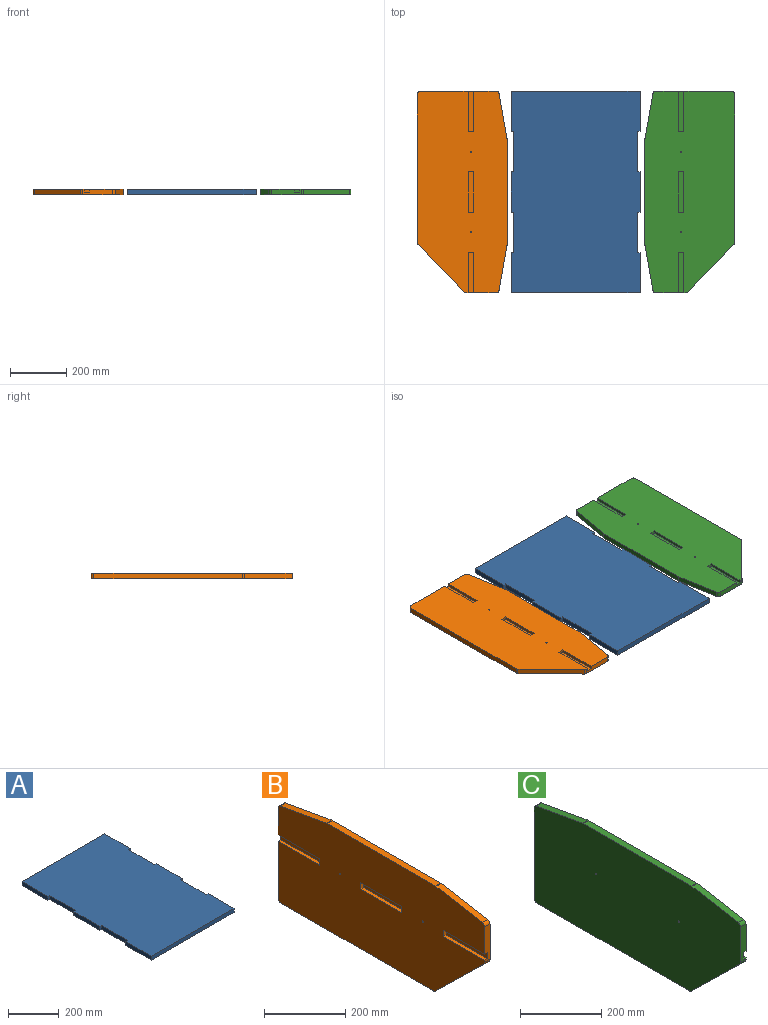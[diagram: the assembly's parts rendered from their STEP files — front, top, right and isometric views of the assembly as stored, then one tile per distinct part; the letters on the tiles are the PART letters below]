
ASSEMBLY  parts=3 mates=2
PART A: 22 faces, bbox 460x720x19 mm
  f0: plane 460x19mm, normal (0,-1,0), area 8740mm2, adj f2,f3,f4,f14
  f1: plane 19x10mm, normal (0,1,0), area 190mm2, adj f2,f3,f4,f5
  f2: plane 144x19mm, normal (-1,0,0), area 2736mm2, adj f0,f1,f3,f4
  f3: plane 720x460mm, normal (0,0,-1), area 325440mm2, adj f0,f1,f2,f5,f6,f7,f8,f9
  f4: plane 720x460mm, normal (0,0,1), area 325440mm2, adj f0,f1,f2,f5,f6,f7,f8,f9
  f5: plane 144x19mm, normal (-1,0,0), area 2736mm2, adj f1,f3,f4,f6
  f6: plane 19x10mm, normal (0,-1,0), area 190mm2, adj f3,f4,f5,f8
  f7: plane 19x10mm, normal (0,1,0), area 190mm2, adj f3,f4,f8,f9
  f8: plane 144x19mm, normal (-1,0,0), area 2736mm2, adj f3,f4,f6,f7
  f9: plane 144x19mm, normal (-1,0,0), area 2736mm2, adj f3,f4,f7,f10
  f10: plane 19x10mm, normal (0,-1,0), area 190mm2, adj f3,f4,f9,f12
  f11: plane 460x19mm, normal (0,1,0), area 8740mm2, adj f3,f4,f12,f21
  f12: plane 144x19mm, normal (-1,0,0), area 2736mm2, adj f3,f4,f10,f11
  f13: plane 19x10mm, normal (0,1,0), area 190mm2, adj f3,f4,f14,f15
  f14: plane 144x19mm, normal (1,0,0), area 2736mm2, adj f0,f3,f4,f13
  f15: plane 144x19mm, normal (1,0,0), area 2736mm2, adj f3,f4,f13,f16
  f16: plane 19x10mm, normal (0,-1,0), area 190mm2, adj f3,f4,f15,f18
  f17: plane 19x10mm, normal (0,1,0), area 190mm2, adj f3,f4,f18,f19
  f18: plane 144x19mm, normal (1,0,0), area 2736mm2, adj f3,f4,f16,f17
  f19: plane 144x19mm, normal (1,0,0), area 2736mm2, adj f3,f4,f17,f20
  f20: plane 19x10mm, normal (0,-1,0), area 190mm2, adj f3,f4,f19,f21
  f21: plane 144x19mm, normal (1,0,0), area 2736mm2, adj f3,f4,f11,f20
PART B: 31 faces, bbox 19x720x320 mm
  f0: plane 720x320mm, normal (-1,0,0), area 202046.2mm2, adj f1,f2,f3,f5,f6,f7,f8,f9
  f1: plane 106.4x19mm, normal (0,-1,0), area 1831.6mm2, adj f0,f4,f11,f14,f26,f27,f28
  f2: plane 377.97x19mm, normal (0,0,1), area 7181.5mm2, adj f0,f4,f9,f12
  f3: plane 530.93x19mm, normal (0,0,-1), area 10087.6mm2, adj f0,f4,f13,f15
  f4: plane 720x320mm, normal (1,0,0), area 210254.2mm2, adj f1,f2,f3,f5,f6,f7,f8,f9
  f5: plane 271.61x19mm, normal (0,1,0), area 4970.6mm2, adj f0,f4,f10,f15,f17,f18,f19
  f6: plane 161.01x28.39mm, normal (0,0.17,0.98), area 3106.4mm2, adj f0,f4,f9,f10
  f7: plane 161.01x28.39mm, normal (0,-0.17,0.98), area 3106.4mm2, adj f0,f4,f11,f12
  f8: plane 169.07x165.21mm, normal (0,-0.7,-0.72), area 4491.4mm2, adj f0,f4,f13,f14
  f9: cylinder r=10mm len=19mm, axis (-1,0,0), area 33.2mm2, adj f0,f2,f4,f6
  f10: cylinder r=10mm len=19mm, axis (1,0,0), area 265.3mm2, adj f0,f4,f5,f6
  f11: cylinder r=10mm len=19mm, axis (-1,0,0), area 265.3mm2, adj f0,f1,f4,f7
  f12: cylinder r=10mm len=19mm, axis (-1,0,0), area 33.2mm2, adj f0,f2,f4,f7
  f13: cylinder r=10mm len=19mm, axis (-1,0,0), area 147mm2, adj f0,f3,f4,f8
  f14: cylinder r=10mm len=19mm, axis (1,0,0), area 151.4mm2, adj f0,f1,f4,f8
  f15: cylinder r=10mm len=19mm, axis (-1,0,0), area 298.5mm2, adj f0,f3,f4,f5
  f16: plane 19x10mm, normal (0,1,0), area 190mm2, adj f0,f17,f18,f19
  f17: plane 144x19mm, normal (-1,0,0), area 2736mm2, adj f5,f16,f18,f19
  f18: plane 144x10mm, normal (0,0,1), area 1440mm2, adj f0,f5,f16,f17
  f19: plane 144x10mm, normal (0,0,-1), area 1440mm2, adj f0,f5,f16,f17
  f20: plane 19x10mm, normal (0,1,0), area 190mm2, adj f0,f22,f23,f24
  f21: plane 19x10mm, normal (0,-1,0), area 190mm2, adj f0,f22,f23,f24
  f22: plane 144x19mm, normal (-1,0,0), area 2736mm2, adj f20,f21,f23,f24
  f23: plane 144x10mm, normal (0,0,1), area 1440mm2, adj f0,f20,f21,f22
  f24: plane 144x10mm, normal (0,0,-1), area 1440mm2, adj f0,f20,f21,f22
  f25: plane 19x10mm, normal (0,-1,0), area 190mm2, adj f0,f26,f27,f28
  f26: plane 144x19mm, normal (-1,0,0), area 2736mm2, adj f1,f25,f27,f28
  f27: plane 144x10mm, normal (0,0,1), area 1440mm2, adj f0,f1,f25,f26
  f28: plane 144x10mm, normal (0,0,-1), area 1440mm2, adj f0,f1,f25,f26
  f29: cylinder r=2mm len=19mm, axis (1,0,0), area 238.8mm2, adj f0,f4
  f30: cylinder r=2mm len=19mm, axis (1,0,0), area 238.8mm2, adj f0,f4
PART C: 31 faces, bbox 19x720x320 mm
  f0: plane 720x320mm, normal (1,0,0), area 202046.2mm2, adj f1,f2,f3,f5,f6,f7,f8,f9
  f1: plane 106.4x19mm, normal (0,-1,0), area 1831.6mm2, adj f0,f4,f11,f14,f26,f27,f28
  f2: plane 377.97x19mm, normal (0,0,1), area 7181.5mm2, adj f0,f4,f9,f12
  f3: plane 530.93x19mm, normal (0,0,-1), area 10087.6mm2, adj f0,f4,f13,f15
  f4: plane 720x320mm, normal (-1,0,0), area 210254.2mm2, adj f1,f2,f3,f5,f6,f7,f8,f9
  f5: plane 271.61x19mm, normal (0,1,0), area 4970.6mm2, adj f0,f4,f10,f15,f17,f18,f19
  f6: plane 161.01x28.39mm, normal (0,0.17,0.98), area 3106.4mm2, adj f0,f4,f9,f10
  f7: plane 161.01x28.39mm, normal (0,-0.17,0.98), area 3106.4mm2, adj f0,f4,f11,f12
  f8: plane 169.07x165.21mm, normal (0,-0.7,-0.72), area 4491.4mm2, adj f0,f4,f13,f14
  f9: cylinder r=10mm len=19mm, axis (1,0,0), area 33.2mm2, adj f0,f2,f4,f6
  f10: cylinder r=10mm len=19mm, axis (-1,0,0), area 265.3mm2, adj f0,f4,f5,f6
  f11: cylinder r=10mm len=19mm, axis (1,0,0), area 265.3mm2, adj f0,f1,f4,f7
  f12: cylinder r=10mm len=19mm, axis (1,0,0), area 33.2mm2, adj f0,f2,f4,f7
  f13: cylinder r=10mm len=19mm, axis (1,0,0), area 147mm2, adj f0,f3,f4,f8
  f14: cylinder r=10mm len=19mm, axis (-1,0,0), area 151.4mm2, adj f0,f1,f4,f8
  f15: cylinder r=10mm len=19mm, axis (1,0,0), area 298.5mm2, adj f0,f3,f4,f5
  f16: plane 19x10mm, normal (0,1,0), area 190mm2, adj f0,f17,f18,f19
  f17: plane 144x19mm, normal (1,0,0), area 2736mm2, adj f5,f16,f18,f19
  f18: plane 144x10mm, normal (0,0,1), area 1440mm2, adj f0,f5,f16,f17
  f19: plane 144x10mm, normal (0,0,-1), area 1440mm2, adj f0,f5,f16,f17
  f20: plane 19x10mm, normal (0,1,0), area 190mm2, adj f0,f22,f23,f24
  f21: plane 19x10mm, normal (0,-1,0), area 190mm2, adj f0,f22,f23,f24
  f22: plane 144x19mm, normal (1,0,0), area 2736mm2, adj f20,f21,f23,f24
  f23: plane 144x10mm, normal (0,0,1), area 1440mm2, adj f0,f20,f21,f22
  f24: plane 144x10mm, normal (0,0,-1), area 1440mm2, adj f0,f20,f21,f22
  f25: plane 19x10mm, normal (0,-1,0), area 190mm2, adj f0,f26,f27,f28
  f26: plane 144x19mm, normal (1,0,0), area 2736mm2, adj f1,f25,f27,f28
  f27: plane 144x10mm, normal (0,0,1), area 1440mm2, adj f0,f1,f25,f26
  f28: plane 144x10mm, normal (0,0,-1), area 1440mm2, adj f0,f1,f25,f26
  f29: cylinder r=2mm len=19mm, axis (1,0,0), area 238.8mm2, adj f0,f4
  f30: cylinder r=2mm len=19mm, axis (1,0,0), area 238.8mm2, adj f0,f4
PLACE A t=(230,0,19)mm
PLACE B rot(axis=(0,1,0),90deg) t=(-134.69,0.04,239)mm
PLACE C rot(axis=(0,-1,0),90deg) t=(597.36,0.04,239)mm
MATE planar B.f0 <-> A.f4  axis (0,0,1) through (-14.69,-359.96,19)mm
MATE planar A.f4 <-> C.f0  axis (0,0,1) through (230,-360,19)mm
